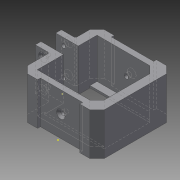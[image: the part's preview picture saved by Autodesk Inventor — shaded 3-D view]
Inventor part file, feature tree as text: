
AUTODESK INVENTOR PART (.ipt)
format: ipt  version: 2015 (Build 190159000, 159)  size: 202,752 bytes
history: native  units: mm
features: sketch x13, extrude x5, hole x5, chamfer x4
ambient origin geometry x8: Origin, YZ Plane, XZ Plane, XY Plane, X Axis, Y Axis, Z Axis, Center Point
bodies: Solid1 (feature_tree)
feature tree (27):
  extrude  "Extrusion1"  Depth=42.5mm
  chamfer  "Chamfer1"  Distance=30.0mm
  chamfer  "Chamfer2"  Distance=5.0mm Angle=45.0deg
  hole  "Hole1"  [1 undecoded]
  extrude  "Extrusion2"  Depth=30.0mm
  sketch  "Sketch4"  dims[d4=6.0mm]
  extrude  "Extrusion3"  Depth=2.0mm
  sketch  "Sketch6"  dims[d11=5.0mm d12=2.0mm d13=45.0deg d14=15.0mm]
  hole  "Hole2"  [1 undecoded]
  hole  "Hole3"  [1 undecoded]
  hole  "Hole4"  [1 undecoded]
  hole  "Hole5"  [1 undecoded]
  extrude  "Extrusion4"  Depth=5.0mm
  sketch  "Sketch12"  dims[d32=10.0mm d33=0.0mm]
  extrude  "Extrusion5"  Depth=5.0mm
  chamfer  "Chamfer3"  Distance=1.5mm
  chamfer  "Chamfer4"  Distance=6.0mm
  sketch  "Sketch1"  dims[d0=42.5mm d1=42.5mm]
  sketch  "Sketch2"  dims[d2=6.0mm]
  sketch  "Sketch3"  dims[d3=6.0mm]
  sketch  "Sketch5"  dims[d5=6.0mm d6=30.0mm d7=0.0mm d8=5.0mm d9=2.0mm d10=45.0deg]
  sketch  "Sketch7"  dims[d15=3.0mm d16=6.0mm d17=4.0mm d18=2.0mm d19=90.0deg d20=100.0mm d21=20.594885mm d22=30.0mm]
  sketch  "Sketch8"  dims[d23=6.25mm d24=2.0mm]
  sketch  "Sketch9"  dims[d25=2.0mm d26=30.0mm d27=0.0mm]
  sketch  "Sketch10"  dims[d28=10.5mm d29=4.0mm]
  sketch  "Sketch11"  dims[d30=4.0mm d31=5.25mm]
  sketch  "Sketch13"  dims[d34=3.0mm d35=6.0mm d36=6.0mm d37=2.0mm d38=90.0deg d39=100.0mm d40=20.594885mm d41=3.0mm d42=6.0mm d43=6.0mm d44=2.0mm d45=90.0deg d46=5.0mm d47=20.594885mm d48=5.0mm d49=5.0mm d50=3.0mm d51=6.0mm d52=6.0mm d53=2.0mm d54=90.0deg d55=5.0mm d56=20.594885mm d57=3.0mm d58=6.0mm d59=6.0mm d60=2.0mm d61=90.0deg d62=5.0mm d63=20.594885mm d64=5.0mm d65=1.5mm d66=0.0mm d67=6.0mm d68=0.0mm d69=1.0mm d70=2.0mm d71=45.0deg d72=1.0mm d73=2.0mm d74=45.0deg]
note: 5 required parameter values undecoded (feature->parameter linkage not recoverable at this tier; creation-order binding heuristic only, values carry confidence <= 0.55)
